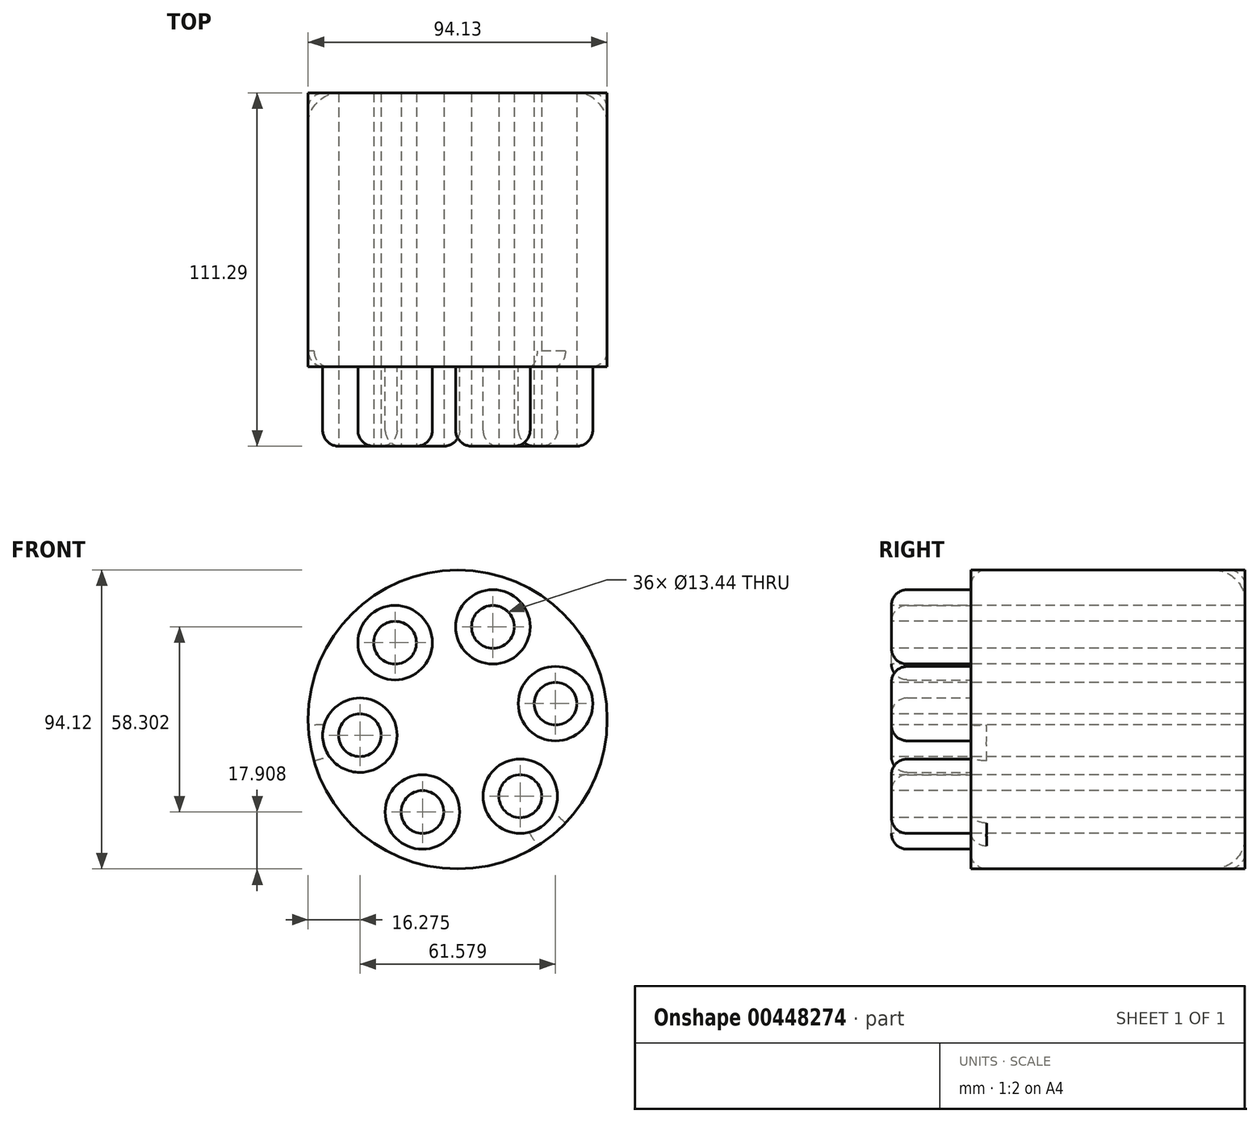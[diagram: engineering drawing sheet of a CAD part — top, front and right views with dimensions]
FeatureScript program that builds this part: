
annotation { "Feature Type Name" : "Feature", "Feature Type Description" : "" }
export const myFeature = defineFeature(function(context is Context, id is Id, definition is map)
    precondition{}
    {
        {
            var Q0;
            Q0=qCreatedBy(makeId("Front.planeOp"),FACE);
            var sketch = newSketch(context, id + "F0", { "sketchPlane" : qUnion([Q0])});
            skCircle(sketch, "E0", {"center": v(-20.43, -35.08) * mm, "radius": 47.06 * mm});
            skSolve(sketch);
        }
        {
            var Q0;
            Q0=makeQuery(id+"F0.imprint","IMPRINT",FACE,{"disambiguationData":[TD([[makeQuery(id+"F0.imprint","IMPRINT",EDGE,{"derivedFrom":sQuery(id+"F0.wireOp",EDGE,"E0")}),1.0]])]});
            extrude(context, id + "F1", {"entities" : qUnion([Q0]), "depth" : 86.3 * mm});
        }
        {
            var Q0;
            Q0=makeQuery(id+"F1.opExtrude","CAP_FACE",FACE,{"disambiguationData":[OSD([sQuery(id+"F0.wireOp",EDGE,"E0")])],"isStart":false});
            var sketch = newSketch(context, id + "F2", { "sketchPlane" : qUnion([Q0])});
            skCircle(sketch, "E1", {"center": v(-51.21, -40.05) * mm, "radius": 11.72 * mm});
            skSolve(sketch);
        }
        {
            var Q0;
            Q0 = qSketchRegion(id + "F2", true);
            extrude(context, id + "F3", {"entities" : qUnion([Q0]), "operationType" : NewBodyOperationType.ADD, "depth" : 25 * mm});
        }
        {
            var Q0;
            Q0=makeQuery(id+"F1.opExtrude","SWEPT_BODY",BODY,{"disambiguationData":[OSD([sQuery(id+"F0.wireOp",EDGE,"E0")])]});
            var Q1;
            Q1=makeQuery(id+"F1.opExtrude","SWEPT_FACE",FACE,{"disambiguationData":[OSD([sQuery(id+"F0.wireOp",EDGE,"E0")])]});
            circularPattern(context, id + "F4", {"entities" : qUnion([Q0]), "axis" : qUnion([Q1]), "angle" : 360 * degree, "instanceCount" : 6, "equalSpace" : true});
        }
        {
            var Q0;
            Q0=makeQuery(id+"F4.opPattern","COPY",EDGE,{"derivedFrom":makeQuery(id+"F1.opExtrude","CAP_EDGE",EDGE,{"disambiguationData":[OSD([sQuery(id+"F0.wireOp",EDGE,"E0")])],"isStart":true}),"instanceName":"4"});
            fillet(context, id + "F5", {"entities" : qUnion([Q0]), "radius" : 10 * mm, "tangentPropagation" : true, "allowEdgeOverflow" : false});
        }
        {
            var Q0;
            Q0=makeQuery(id+"F4.opPattern","COPY",EDGE,{"derivedFrom":makeQuery(id+"F3.opExtrude","CAP_EDGE",EDGE,{"disambiguationData":[OSD([sQuery(id+"F2.wireOp",EDGE,"E1")])],"isStart":false}),"instanceName":"4"});
            var Q1;
            Q1=makeQuery(id+"F4.opPattern","COPY",FACE,{"derivedFrom":makeQuery(id+"F3.opExtrude","CAP_FACE",FACE,{"disambiguationData":[OSD([sQuery(id+"F2.wireOp",EDGE,"E1")])],"isStart":false}),"instanceName":"3"});
            var Q2;
            Q2=makeQuery(id+"F4.opPattern","COPY",FACE,{"derivedFrom":makeQuery(id+"F3.opExtrude","CAP_FACE",FACE,{"disambiguationData":[OSD([sQuery(id+"F2.wireOp",EDGE,"E1")])],"isStart":false}),"instanceName":"1"});
            var Q3;
            Q3=makeQuery(id+"F4.opPattern","COPY",EDGE,{"derivedFrom":makeQuery(id+"F3.opExtrude","CAP_EDGE",EDGE,{"disambiguationData":[OSD([sQuery(id+"F2.wireOp",EDGE,"E1")])],"isStart":false}),"instanceName":"2"});
            var Q4;
            Q4=makeQuery(id+"F3.opExtrude","CAP_FACE",FACE,{"disambiguationData":[OSD([sQuery(id+"F2.wireOp",EDGE,"E1")])],"isStart":false});
            var Q5;
            Q5=makeQuery(id+"F4.opPattern","COPY",EDGE,{"derivedFrom":makeQuery(id+"F3.opExtrude","CAP_EDGE",EDGE,{"disambiguationData":[OSD([sQuery(id+"F2.wireOp",EDGE,"E1")])],"isStart":false}),"instanceName":"5"});
            var Q6;
            Q6=makeQuery(id+"F4.opPattern","COPY",EDGE,{"derivedFrom":makeQuery(id+"F1.opExtrude","CAP_EDGE",EDGE,{"disambiguationData":[OSD([sQuery(id+"F0.wireOp",EDGE,"E0")])],"isStart":false}),"instanceName":"4"});
            var Q7;
            Q7=makeQuery(id+"F4.opPattern","COPY",FACE,{"derivedFrom":makeQuery(id+"F1.opExtrude","CAP_FACE",FACE,{"disambiguationData":[OSD([sQuery(id+"F0.wireOp",EDGE,"E0")])],"isStart":true}),"instanceName":"4"});
            var Q8;
            Q8=makeQuery(id+"F1.opExtrude","SWEPT_FACE",FACE,{"disambiguationData":[OSD([sQuery(id+"F0.wireOp",EDGE,"E0")])]});
            fillet(context, id + "F6", {"entities" : qUnion([Q0, Q1, Q2, Q3, Q4, Q5, Q6, Q7, Q8]), "radius" : 5 * mm, "tangentPropagation" : true, "allowEdgeOverflow" : false});
        }
        {
            var Q0;
            Q0=makeQuery(id+"F3.opExtrude","CAP_FACE",FACE,{"disambiguationData":[OSD([sQuery(id+"F2.wireOp",EDGE,"E1")])],"isStart":false});
            var Q1;
            Q1=makeQuery(id+"F4.opPattern","COPY",FACE,{"derivedFrom":makeQuery(id+"F3.opExtrude","CAP_FACE",FACE,{"disambiguationData":[OSD([sQuery(id+"F2.wireOp",EDGE,"E1")])],"isStart":false}),"instanceName":"5"});
            var Q2;
            Q2=makeQuery(id+"F4.opPattern","COPY",FACE,{"derivedFrom":makeQuery(id+"F3.opExtrude","CAP_FACE",FACE,{"disambiguationData":[OSD([sQuery(id+"F2.wireOp",EDGE,"E1")])],"isStart":false}),"instanceName":"4"});
            var Q3;
            Q3=makeQuery(id+"F4.opPattern","COPY",FACE,{"derivedFrom":makeQuery(id+"F3.opExtrude","CAP_FACE",FACE,{"disambiguationData":[OSD([sQuery(id+"F2.wireOp",EDGE,"E1")])],"isStart":false}),"instanceName":"3"});
            var Q4;
            Q4=makeQuery(id+"F4.opPattern","COPY",FACE,{"derivedFrom":makeQuery(id+"F3.opExtrude","CAP_FACE",FACE,{"disambiguationData":[OSD([sQuery(id+"F2.wireOp",EDGE,"E1")])],"isStart":false}),"instanceName":"2"});
            var Q5;
            Q5=makeQuery(id+"F4.opPattern","COPY",FACE,{"derivedFrom":makeQuery(id+"F3.opExtrude","CAP_FACE",FACE,{"disambiguationData":[OSD([sQuery(id+"F2.wireOp",EDGE,"E1")])],"isStart":false}),"instanceName":"1"});
            extrude(context, id + "F7", {"entities" : qUnion([Q0, Q1, Q2, Q3, Q4, Q5]), "operationType" : NewBodyOperationType.REMOVE, "endBound" : BoundingType.THROUGH_ALL, "oppositeDirection" : true, "depth" : 25 * mm});
        }
    });
